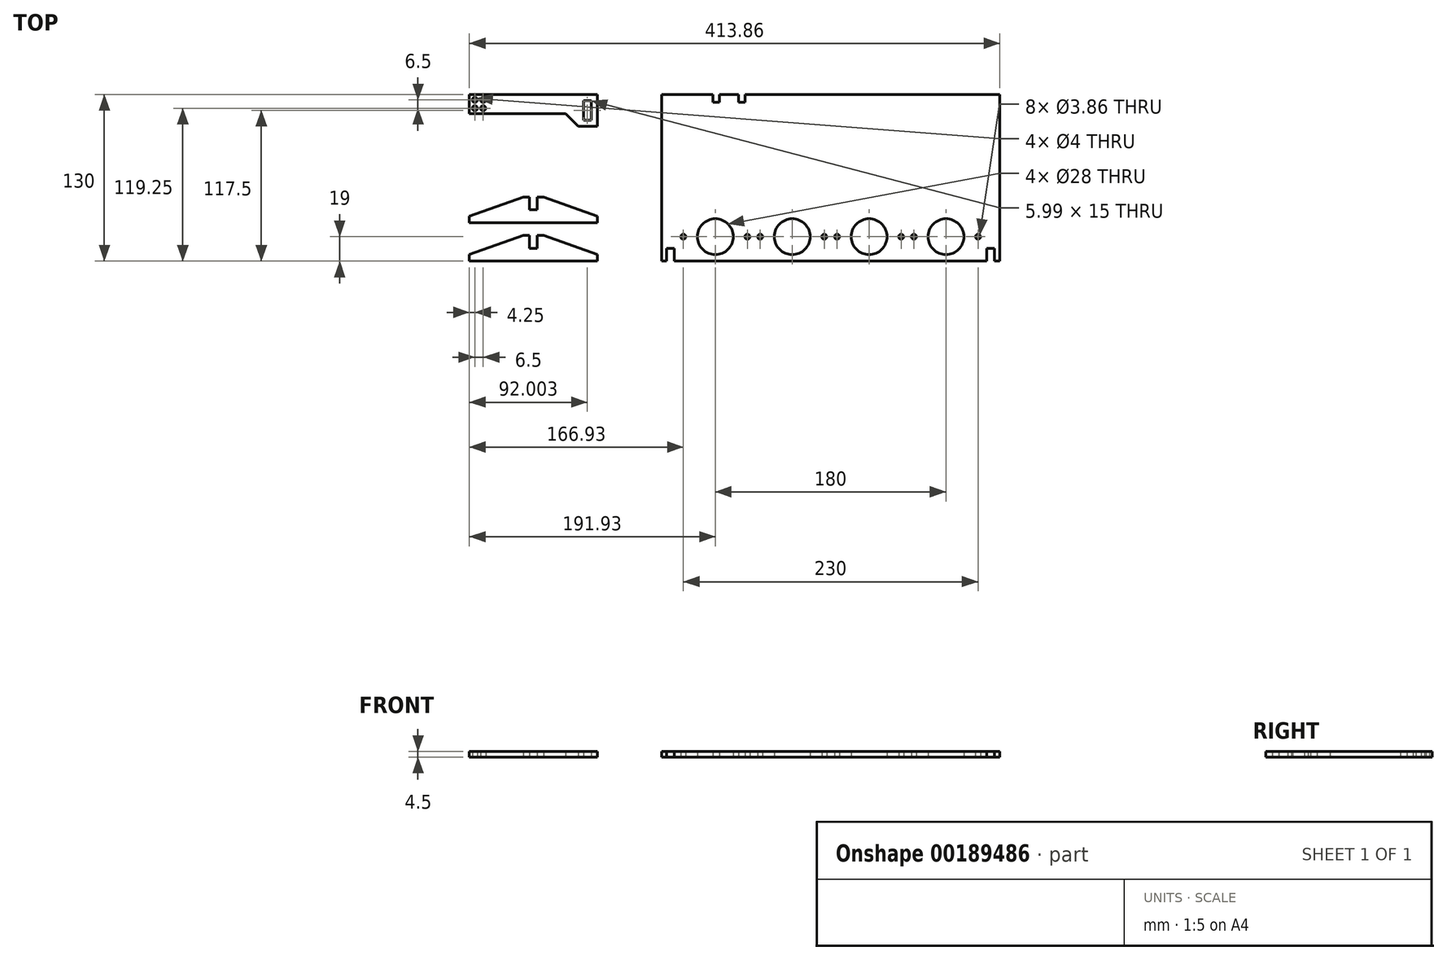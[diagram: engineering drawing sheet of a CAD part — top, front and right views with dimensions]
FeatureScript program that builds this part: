
annotation { "Feature Type Name" : "Feature", "Feature Type Description" : "" }
export const myFeature = defineFeature(function(context is Context, id is Id, definition is map)
    precondition{}
    {
        {
            var Q0;
            Q0=qCreatedBy(makeId("Top.planeOp"),FACE);
            var sketch = newSketch(context, id + "F0", { "sketchPlane" : qUnion([Q0])});
            skCircle(sketch, "E0", {"center": v(41.93, 19) * mm, "radius": 13.5 * mm, "construction": true});
            skLineSegment(sketch, "E1", {"start": v(16.93, 19) * mm, "end": v(66.93, 19) * mm, "construction": true});
            skCircle(sketch, "E2", {"center": v(16.93, 19) * mm, "radius": 1.93 * mm});
            skCircle(sketch, "E3", {"center": v(41.93, 19) * mm, "radius": 14 * mm});
            skCircle(sketch, "E4", {"center": v(66.93, 19) * mm, "radius": 1.93 * mm});
            skPoint(sketch, "E5", {"position": v(41.93, 5) * mm});
            skPoint(sketch, "E6", {"position": v(15, 19) * mm});
            skLineSegment(sketch, "E7.bottom", {"start": v(0, 0) * mm, "end": v(4, 0) * mm});
            skLineSegment(sketch, "E7.top", {"start": v(0, 130) * mm, "end": v(40, 130) * mm});
            skLineSegment(sketch, "E7.left", {"start": v(0, 0) * mm, "end": v(0, 130) * mm});
            skLineSegment(sketch, "E7.right", {"start": v(263.86, 0) * mm, "end": v(263.86, 130) * mm});
            skPoint(sketch, "E8.1.0.0", {"position": v(101.93, 5) * mm});
            skPoint(sketch, "E8.1.0.1", {"position": v(75, 19) * mm});
            skCircle(sketch, "E8.1.0.2", {"center": v(101.93, 19) * mm, "radius": 14 * mm});
            skLineSegment(sketch, "E8.1.0.3", {"start": v(76.93, 19) * mm, "end": v(126.93, 19) * mm, "construction": true});
            skCircle(sketch, "E8.1.0.4", {"center": v(101.93, 19) * mm, "radius": 13.5 * mm, "construction": true});
            skCircle(sketch, "E8.1.0.5", {"center": v(126.93, 19) * mm, "radius": 1.93 * mm});
            skCircle(sketch, "E8.1.0.6", {"center": v(76.93, 19) * mm, "radius": 1.93 * mm});
            skPoint(sketch, "E8.2.0.0", {"position": v(161.93, 5) * mm});
            skPoint(sketch, "E8.2.0.1", {"position": v(135, 19) * mm});
            skCircle(sketch, "E8.2.0.2", {"center": v(161.93, 19) * mm, "radius": 14 * mm});
            skLineSegment(sketch, "E8.2.0.3", {"start": v(136.93, 19) * mm, "end": v(186.93, 19) * mm, "construction": true});
            skCircle(sketch, "E8.2.0.4", {"center": v(161.93, 19) * mm, "radius": 13.5 * mm, "construction": true});
            skCircle(sketch, "E8.2.0.5", {"center": v(186.93, 19) * mm, "radius": 1.93 * mm});
            skCircle(sketch, "E8.2.0.6", {"center": v(136.93, 19) * mm, "radius": 1.93 * mm});
            skPoint(sketch, "E8.3.0.0", {"position": v(221.93, 5) * mm});
            skPoint(sketch, "E8.3.0.1", {"position": v(195, 19) * mm});
            skCircle(sketch, "E8.3.0.2", {"center": v(221.93, 19) * mm, "radius": 14 * mm});
            skLineSegment(sketch, "E8.3.0.3", {"start": v(196.93, 19) * mm, "end": v(246.93, 19) * mm, "construction": true});
            skCircle(sketch, "E8.3.0.4", {"center": v(221.93, 19) * mm, "radius": 13.5 * mm, "construction": true});
            skCircle(sketch, "E8.3.0.5", {"center": v(246.93, 19) * mm, "radius": 1.93 * mm});
            skCircle(sketch, "E8.3.0.6", {"center": v(196.93, 19) * mm, "radius": 1.93 * mm});
            skLineSegment(sketch, "E8.direction1", {"start": v(15, 19) * mm, "end": v(75, 19) * mm, "construction": true});
            skPoint(sketch, "E9", {"position": v(248.86, 19) * mm});
            skLineSegment(sketch, "E10", {"start": v(-50, 0) * mm, "end": v(-150, 0) * mm});
            skLineSegment(sketch, "E11", {"start": v(-150, 0) * mm, "end": v(-150, 5) * mm});
            skLineSegment(sketch, "E12", {"start": v(-150, 5) * mm, "end": v(-108, 20) * mm});
            skLineSegment(sketch, "E13", {"start": v(-108, 20) * mm, "end": v(-103, 20) * mm});
            skLineSegment(sketch, "E14", {"start": v(-103, 20) * mm, "end": v(-103, 10) * mm});
            skLineSegment(sketch, "E15", {"start": v(-103, 10) * mm, "end": v(-97, 10) * mm});
            skLineSegment(sketch, "E16", {"start": v(-97, 10) * mm, "end": v(-97, 20) * mm});
            skLineSegment(sketch, "E17", {"start": v(-97, 20) * mm, "end": v(-92, 20) * mm});
            skLineSegment(sketch, "E18", {"start": v(-92, 20) * mm, "end": v(-50, 5) * mm});
            skLineSegment(sketch, "E19", {"start": v(-50, 5) * mm, "end": v(-50, 0) * mm});
            skPoint(sketch, "E20", {"position": v(-100, 0) * mm});
            skPoint(sketch, "E21", {"position": v(-100, 10) * mm});
            skLineSegment(sketch, "E22", {"start": v(4, 0) * mm, "end": v(4, 10) * mm});
            skLineSegment(sketch, "E23", {"start": v(4, 10) * mm, "end": v(10, 10) * mm});
            skLineSegment(sketch, "E24", {"start": v(10, 10) * mm, "end": v(10, 0) * mm});
            skLineSegment(sketch, "E25.trimOffspring", {"start": v(10, 0) * mm, "end": v(253.87, 0) * mm});
            skLineSegment(sketch, "E26", {"start": v(-100, 10) * mm, "end": v(-100, 0) * mm, "construction": true});
            skLineSegment(sketch, "E27", {"start": v(259.86, 0) * mm, "end": v(259.86, 10) * mm});
            skLineSegment(sketch, "E28", {"start": v(259.86, 10) * mm, "end": v(253.87, 10) * mm});
            skLineSegment(sketch, "E29", {"start": v(253.87, 10) * mm, "end": v(253.87, 0) * mm});
            skLineSegment(sketch, "E30.trimOffspring", {"start": v(259.86, 0) * mm, "end": v(263.86, 0) * mm});
            skPoint(sketch, "E31", {"position": v(41.93, 33) * mm});
            skLineSegment(sketch, "E32.0.1.0", {"start": v(-92, 50) * mm, "end": v(-50, 35) * mm});
            skPoint(sketch, "E32.0.1.1", {"position": v(-100, 30) * mm});
            skLineSegment(sketch, "E32.0.1.2", {"start": v(-103, 50) * mm, "end": v(-103, 40) * mm});
            skLineSegment(sketch, "E32.0.1.3", {"start": v(-100, 40) * mm, "end": v(-100, 30) * mm, "construction": true});
            skLineSegment(sketch, "E32.0.1.4", {"start": v(-150, 35) * mm, "end": v(-108, 50) * mm});
            skPoint(sketch, "E32.0.1.5", {"position": v(-100, 40) * mm});
            skLineSegment(sketch, "E32.0.1.6", {"start": v(-50, 30) * mm, "end": v(-150, 30) * mm});
            skLineSegment(sketch, "E32.0.1.7", {"start": v(-97, 40) * mm, "end": v(-97, 50) * mm});
            skLineSegment(sketch, "E32.0.1.8", {"start": v(-103, 40) * mm, "end": v(-97, 40) * mm});
            skLineSegment(sketch, "E32.0.1.9", {"start": v(-108, 50) * mm, "end": v(-103, 50) * mm});
            skLineSegment(sketch, "E32.0.1.10", {"start": v(-97, 50) * mm, "end": v(-92, 50) * mm});
            skLineSegment(sketch, "E32.0.1.11", {"start": v(-150, 30) * mm, "end": v(-150, 35) * mm});
            skLineSegment(sketch, "E32.0.1.12", {"start": v(-50, 35) * mm, "end": v(-50, 30) * mm});
            skLineSegment(sketch, "E32.direction1", {"start": v(-150, 0) * mm, "end": v(-125, 0) * mm, "construction": true});
            skLineSegment(sketch, "E32.direction2", {"start": v(-150, 0) * mm, "end": v(-150, 30) * mm, "construction": true});
            skLineSegment(sketch, "E33.bottom", {"start": v(258.86, 125) * mm, "end": v(88.86, 125) * mm, "construction": true});
            skLineSegment(sketch, "E33.top", {"start": v(258.86, 70) * mm, "end": v(88.86, 70) * mm, "construction": true});
            skLineSegment(sketch, "E33.left", {"start": v(258.86, 125) * mm, "end": v(258.86, 70) * mm, "construction": true});
            skLineSegment(sketch, "E33.right", {"start": v(88.86, 125) * mm, "end": v(88.86, 70) * mm, "construction": true});
            skLineSegment(sketch, "E34", {"start": v(-50, 130) * mm, "end": v(-50, 105) * mm});
            skLineSegment(sketch, "E35", {"start": v(-50, 105) * mm, "end": v(-65, 105) * mm});
            skLineSegment(sketch, "E36", {"start": v(-65, 105) * mm, "end": v(-75, 115) * mm});
            skLineSegment(sketch, "E37", {"start": v(-75, 115) * mm, "end": v(-150, 115) * mm});
            skLineSegment(sketch, "E38", {"start": v(-150, 115) * mm, "end": v(-150, 130) * mm});
            skLineSegment(sketch, "E39", {"start": v(-150, 130) * mm, "end": v(-50, 130) * mm});
            skLineSegment(sketch, "E40.bottom", {"start": v(-55, 125) * mm, "end": v(-61, 125) * mm});
            skLineSegment(sketch, "E40.top", {"start": v(-55, 110) * mm, "end": v(-61, 110) * mm});
            skLineSegment(sketch, "E40.left", {"start": v(-55, 125) * mm, "end": v(-55, 110) * mm});
            skLineSegment(sketch, "E40.right", {"start": v(-61, 125) * mm, "end": v(-61, 110) * mm});
            skLineSegment(sketch, "E41", {"start": v(40, 130) * mm, "end": v(40, 124) * mm});
            skLineSegment(sketch, "E42", {"start": v(40, 124) * mm, "end": v(45, 124) * mm});
            skLineSegment(sketch, "E43", {"start": v(45, 124) * mm, "end": v(45, 130) * mm});
            skLineSegment(sketch, "E44", {"start": v(60, 130) * mm, "end": v(60, 124) * mm});
            skLineSegment(sketch, "E45", {"start": v(60, 124) * mm, "end": v(65, 124) * mm});
            skLineSegment(sketch, "E46", {"start": v(65, 124) * mm, "end": v(65, 130) * mm});
            skLineSegment(sketch, "E47.trimOffspring", {"start": v(45, 130) * mm, "end": v(60, 130) * mm});
            skLineSegment(sketch, "E48.trimOffspring", {"start": v(65, 130) * mm, "end": v(263.86, 130) * mm});
            skCircle(sketch, "E49", {"center": v(-145.75, 125.75) * mm, "radius": 2 * mm});
            skCircle(sketch, "E50", {"center": v(-139.25, 125.75) * mm, "radius": 2 * mm});
            skCircle(sketch, "E51", {"center": v(-139.25, 119.25) * mm, "radius": 2 * mm});
            skCircle(sketch, "E52", {"center": v(-145.75, 119.25) * mm, "radius": 2 * mm});
            skLineSegment(sketch, "E53.bottom", {"start": v(-145.75, 125.75) * mm, "end": v(-139.25, 125.75) * mm, "construction": true});
            skLineSegment(sketch, "E53.top", {"start": v(-145.75, 119.25) * mm, "end": v(-139.25, 119.25) * mm, "construction": true});
            skLineSegment(sketch, "E53.left", {"start": v(-145.75, 125.75) * mm, "end": v(-145.75, 119.25) * mm, "construction": true});
            skLineSegment(sketch, "E53.right", {"start": v(-139.25, 125.75) * mm, "end": v(-139.25, 119.25) * mm, "construction": true});
            skLineSegment(sketch, "E54", {"start": v(-145.75, 125.75) * mm, "end": v(-145.75, 130) * mm, "construction": true});
            skLineSegment(sketch, "E55", {"start": v(-145.75, 125.75) * mm, "end": v(-150, 125.75) * mm, "construction": true});
            skLineSegment(sketch, "E56", {"start": v(-145.75, 119.25) * mm, "end": v(-145.75, 115) * mm, "construction": true});
            skSolve(sketch);
        }
        {
            var Q0;
            Q0 = qSketchRegion(id + "F0", true);
            extrude(context, id + "F1", {"entities" : qUnion([Q0]), "depth" : 4.5 * mm});
        }
    });
